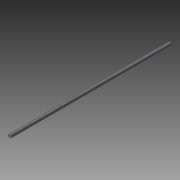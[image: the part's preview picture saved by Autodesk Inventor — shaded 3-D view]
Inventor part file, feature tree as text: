
AUTODESK INVENTOR PART (.ipt)
format: ipt  version: 2015 (Build 190159000, 159)  size: 68,096 bytes
history: native  units: in
note: dims shown in document units (in); Inventor stores cm internally (conversion verified against a paired STEP export)
features: extrude x1, thread x1, sketch x1
ambient origin geometry x8: Origin, YZ Plane, XZ Plane, XY Plane, X Axis, Y Axis, Z Axis, Center Point
bodies: Solid1 (feature_tree)
feature tree (3):
  extrude  "Extrusion1"  Depth=16.0in TaperAngle=0.0deg
  thread  "Thread1"  [1 undecoded]
  sketch  "Sketch1"  dims[d0=0.375in d1=16.0in d2=0.0in d3=1.0in d4=0.0in]
note: 1 required parameter value undecoded (feature->parameter linkage not recoverable at this tier; creation-order binding heuristic only, values carry confidence <= 0.55)
